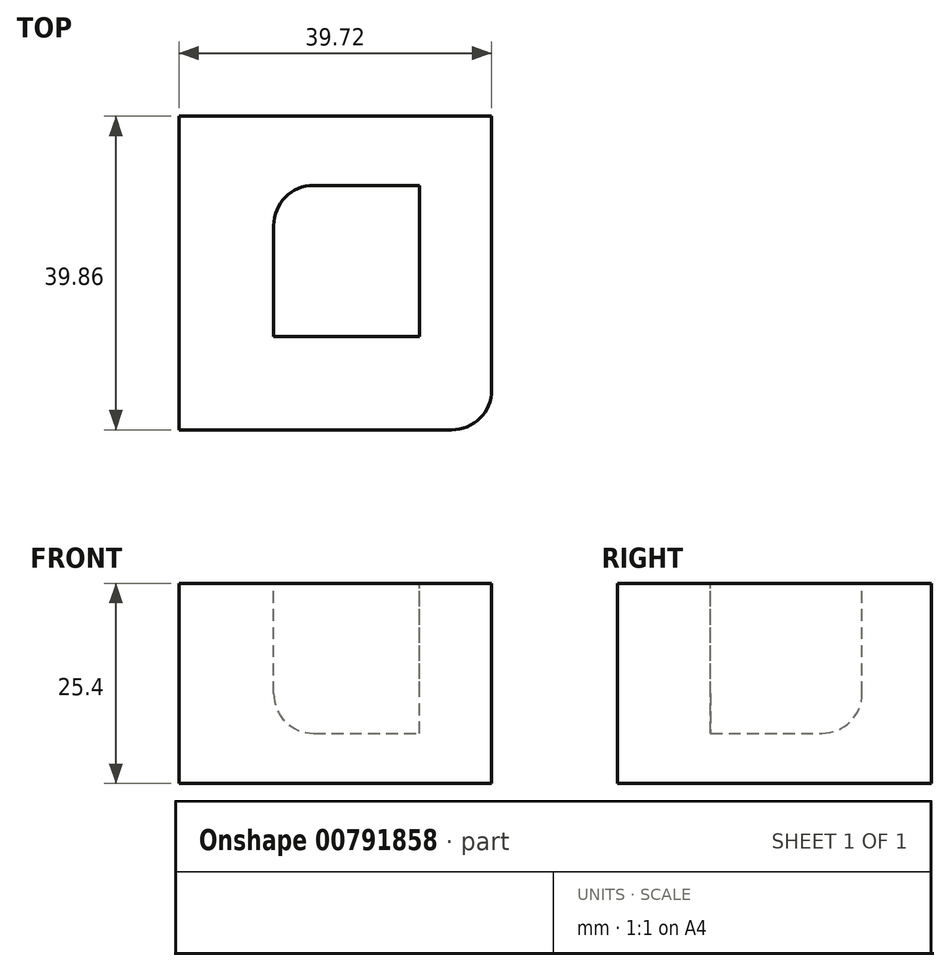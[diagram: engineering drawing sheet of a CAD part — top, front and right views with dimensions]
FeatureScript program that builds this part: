
annotation { "Feature Type Name" : "Feature", "Feature Type Description" : "" }
export const myFeature = defineFeature(function(context is Context, id is Id, definition is map)
    precondition{}
    {
        {
            var Q0;
            Q0=qCreatedBy(makeId("Top.planeOp"),FACE);
            var sketch = newSketch(context, id + "F0", { "sketchPlane" : qUnion([Q0])});
            skLineSegment(sketch, "E0.bottom", {"start": v(0, 0) * mm, "end": v(39.72, 0) * mm});
            skLineSegment(sketch, "E0.top", {"start": v(0, 39.86) * mm, "end": v(39.72, 39.86) * mm});
            skLineSegment(sketch, "E0.left", {"start": v(0, 0) * mm, "end": v(0, 39.86) * mm});
            skLineSegment(sketch, "E0.right", {"start": v(39.72, 0) * mm, "end": v(39.72, 39.86) * mm});
            skSolve(sketch);
        }
        {
            var Q0;
            Q0 = qSketchRegion(id + "F0", true);
            extrude(context, id + "F1", {"entities" : qUnion([Q0]), "depth" : 25.4 * mm, "offsetDistance" : 25.4 * mm});
        }
        {
            var Q0;
            Q0=makeQuery(id+"F1.opExtrude","CAP_FACE",FACE,{"disambiguationData":[OSD([sQuery(id+"F0.wireOp",EDGE,"E0.bottom"),sQuery(id+"F0.wireOp",EDGE,"E0.top"),sQuery(id+"F0.wireOp",EDGE,"E0.left"),sQuery(id+"F0.wireOp",EDGE,"E0.right")])],"isStart":false});
            var sketch = newSketch(context, id + "F2", { "sketchPlane" : qUnion([Q0])});
            skLineSegment(sketch, "E1.bottom", {"start": v(12.04, 11.83) * mm, "end": v(30.56, 11.83) * mm});
            skLineSegment(sketch, "E1.top", {"start": v(12.04, 31.06) * mm, "end": v(30.56, 31.06) * mm});
            skLineSegment(sketch, "E1.left", {"start": v(12.04, 11.83) * mm, "end": v(12.04, 31.06) * mm});
            skLineSegment(sketch, "E1.right", {"start": v(30.56, 11.83) * mm, "end": v(30.56, 31.06) * mm});
            skSolve(sketch);
        }
        {
            var Q0;
            Q0 = qSketchRegion(id + "F2", true);
            extrude(context, id + "F3", {"entities" : qUnion([Q0]), "operationType" : NewBodyOperationType.REMOVE, "oppositeDirection" : true, "depth" : 19.05 * mm, "offsetDistance" : 25.4 * mm});
        }
        {
            var Q0;
            Q0=makeQuery(id+"F3.boolean.opBoolean","COPY",EDGE,{"derivedFrom":makeQuery(id+"F3.opExtrude","CAP_EDGE",EDGE,{"disambiguationData":[OSD([sQuery(id+"F2.wireOp",EDGE,"E1.left")])],"isStart":false})});
            var Q1;
            Q1=makeQuery(id+"F3.boolean.opBoolean","COPY",EDGE,{"derivedFrom":makeQuery(id+"F3.opExtrude","SWEPT_EDGE",EDGE,{"disambiguationData":[OSD([sQuery(id+"F2.wireOp",EDGE,"E1.top"),sQuery(id+"F2.wireOp",EDGE,"E1.left")])]})});
            var Q2;
            Q2=makeQuery(id+"F3.boolean.opBoolean","COPY",EDGE,{"derivedFrom":makeQuery(id+"F3.opExtrude","CAP_EDGE",EDGE,{"disambiguationData":[OSD([sQuery(id+"F2.wireOp",EDGE,"E1.top")])],"isStart":false})});
            var Q3;
            Q3=makeQuery(id+"F1.opExtrude","SWEPT_EDGE",EDGE,{"disambiguationData":[OSD([sQuery(id+"F0.wireOp",EDGE,"E0.bottom"),sQuery(id+"F0.wireOp",EDGE,"E0.right")])]});
            fillet(context, id + "F4", {"entities" : qUnion([Q0, Q1, Q2, Q3]), "radius" : 5.08 * mm, "tangentPropagation" : true, "allowEdgeOverflow" : false});
        }
    });
